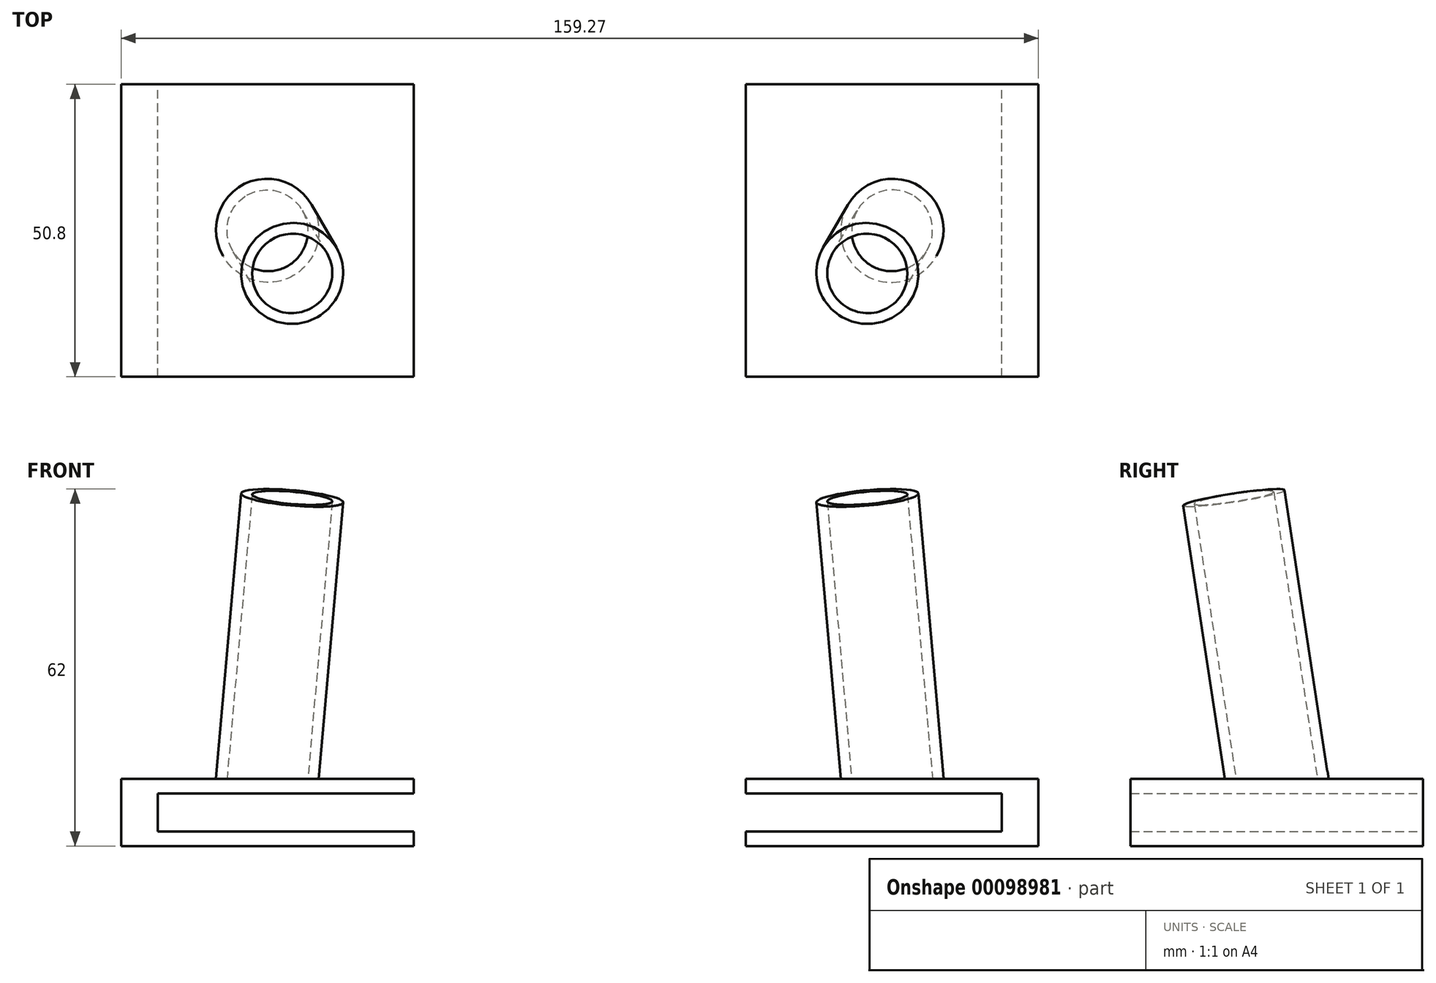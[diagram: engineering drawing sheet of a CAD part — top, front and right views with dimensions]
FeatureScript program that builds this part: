
annotation { "Feature Type Name" : "Feature", "Feature Type Description" : "" }
export const myFeature = defineFeature(function(context is Context, id is Id, definition is map)
    precondition{}
    {
        {
            var Q0;
            Q0=qCreatedBy(makeId("Top.planeOp"),FACE);
            var sketch = newSketch(context, id + "F0", { "sketchPlane" : qUnion([Q0])});
            skLineSegment(sketch, "E0.bottom", {"start": v(25.4, 25.4) * mm, "end": v(-25.4, 25.4) * mm});
            skLineSegment(sketch, "E0.top", {"start": v(25.4, -25.4) * mm, "end": v(-25.4, -25.4) * mm});
            skLineSegment(sketch, "E0.left", {"start": v(25.4, 25.4) * mm, "end": v(25.4, -25.4) * mm});
            skLineSegment(sketch, "E0.right", {"start": v(-25.4, 25.4) * mm, "end": v(-25.4, -25.4) * mm});
            skPoint(sketch, "E0.middle", {"position": v(0, 0) * mm});
            skSolve(sketch);
        }
        {
            var Q0;
            Q0=qSketchRegion(id+"F0",true);
            extrude(context, id + "F1", {"entities" : qUnion([Q0]), "oppositeDirection" : true, "depth" : 2.54 * mm});
        }
        {
            var Q0;
            Q0=makeQuery(id+"F1.opExtrude","CAP_FACE",FACE,{"disambiguationData":[OSD([sQuery(id+"F0.wireOp",EDGE,"E0.bottom"),sQuery(id+"F0.wireOp",EDGE,"E0.top"),sQuery(id+"F0.wireOp",EDGE,"E0.left"),sQuery(id+"F0.wireOp",EDGE,"E0.right")])],"isStart":false});
            var sketch = newSketch(context, id + "F2", { "sketchPlane" : qUnion([Q0])});
            skLineSegment(sketch, "E1.bottom", {"start": v(25.4, 25.4) * mm, "end": v(19.05, 25.4) * mm});
            skLineSegment(sketch, "E1.top", {"start": v(25.4, -25.4) * mm, "end": v(19.05, -25.4) * mm});
            skLineSegment(sketch, "E1.left", {"start": v(25.4, 25.4) * mm, "end": v(25.4, -25.4) * mm});
            skLineSegment(sketch, "E1.right", {"start": v(19.05, 25.4) * mm, "end": v(19.05, -25.4) * mm});
            skSolve(sketch);
        }
        {
            var Q0;
            Q0=qSketchRegion(id+"F2",true);
            extrude(context, id + "F3", {"entities" : qUnion([Q0]), "operationType" : NewBodyOperationType.ADD, "depth" : 6.6 * mm});
        }
        {
            var Q0;
            Q0=makeQuery(id+"F3.opExtrude","CAP_FACE",FACE,{"disambiguationData":[OSD([sQuery(id+"F2.wireOp",EDGE,"E1.bottom"),sQuery(id+"F2.wireOp",EDGE,"E1.top"),sQuery(id+"F2.wireOp",EDGE,"E1.left"),sQuery(id+"F2.wireOp",EDGE,"E1.right")])],"isStart":false});
            var sketch = newSketch(context, id + "F4", { "sketchPlane" : qUnion([Q0])});
            skLineSegment(sketch, "E2.bottom", {"start": v(25.4, 25.4) * mm, "end": v(-25.4, 25.4) * mm});
            skLineSegment(sketch, "E2.top", {"start": v(25.4, -25.4) * mm, "end": v(-25.4, -25.4) * mm});
            skLineSegment(sketch, "E2.left", {"start": v(25.4, 25.4) * mm, "end": v(25.4, -25.4) * mm});
            skLineSegment(sketch, "E2.right", {"start": v(-25.4, 25.4) * mm, "end": v(-25.4, -25.4) * mm});
            skSolve(sketch);
        }
        {
            var Q0;
            Q0=qSketchRegion(id+"F4",true);
            extrude(context, id + "F5", {"entities" : qUnion([Q0]), "operationType" : NewBodyOperationType.ADD, "depth" : 2.54 * mm});
        }
        {
            var Q0;
            Q0=makeQuery(id+"F1.opExtrude","CAP_FACE",FACE,{"disambiguationData":[OSD([sQuery(id+"F0.wireOp",EDGE,"E0.bottom"),sQuery(id+"F0.wireOp",EDGE,"E0.top"),sQuery(id+"F0.wireOp",EDGE,"E0.left"),sQuery(id+"F0.wireOp",EDGE,"E0.right")])],"isStart":true});
            var sketch = newSketch(context, id + "F6", { "sketchPlane" : qUnion([Q0])});
            skLineSegment(sketch, "E3", {"start": v(0, 25.4) * mm, "end": v(0, -28.09) * mm, "construction": true});
            skPoint(sketch, "E3.endSnap0", {"position": v(0, -25.4) * mm});
            skSolve(sketch);
        }
        {
            var Q0;
            Q0=qCreatedBy(makeId("Right.planeOp"),FACE);
            var sketch = newSketch(context, id + "F7", { "sketchPlane" : qUnion([Q0])});
            skLineSegment(sketch, "E4", {"start": v(0, 55.88) * mm, "end": v(0, -47.56) * mm, "construction": true});
            skSolve(sketch);
        }
        {
            var Q0;
            Q0=sQuery(id+"F6.wireOp",EDGE,"E3");
            cPlane(context, id + "F8", {"entities" : qUnion([Q0]), "cplaneType" : CPlaneType.LINE_ANGLE, "offset" : 152.4 * mm, "angle" : 10 * degree, "width" : 152.4 * mm, "height" : 152.4 * mm});
        }
        {
            var Q0;
            Q0=qCreatedBy(id+"F8.planeOp",FACE);
            var sketch = newSketch(context, id + "F9", { "sketchPlane" : qUnion([Q0])});
            skCircle(sketch, "E5", {"center": v(0, 0) * mm, "radius": 6.99 * mm});
            skCircle(sketch, "E6", {"center": v(0, 0) * mm, "radius": 8.9 * mm});
            skSolve(sketch);
        }
        {
            var Q0;
            Q0=qSketchRegion(id+"F9",true);
            extrude(context, id + "F10", {"entities" : qUnion([Q0]), "oppositeDirection" : true, "depth" : 49.53 * mm});
        }
        {
            var Q0;
            Q0=makeQuery(id+"F10.opExtrude","SWEPT_BODY",BODY,{"disambiguationData":[OSD([sQuery(id+"F9.wireOp",EDGE,"E5"),sQuery(id+"F9.wireOp",EDGE,"E6")])]});
            var Q1;
            Q1=sQuery(id+"F7.wireOp",EDGE,"E4");
            transform(context, id + "F11", {"entities" : qUnion([Q0]), "transformType" : TransformType.ROTATION, "transformAxis" : qUnion([Q1]), "angle" : 60 * degree, "oppositeDirection" : true, "makeCopy" : false});
        }
        {
            var Q0;
            Q0=qCreatedBy(makeId("Top.planeOp"),FACE);
            var sketch = newSketch(context, id + "F12", { "sketchPlane" : qUnion([Q0])});
            skLineSegment(sketch, "E7", {"start": v(-54.24, 36.53) * mm, "end": v(-54.24, -61.05) * mm, "construction": true});
            skSolve(sketch);
        }
        {
            var Q0;
            Q0=qCreatedBy(makeId("Right.planeOp"),FACE);
            var sketch = newSketch(context, id + "F13", { "sketchPlane" : qUnion([Q0])});
            skLineSegment(sketch, "E8", {"start": v(8.85, -52.8) * mm, "end": v(8.85, 70.73) * mm, "construction": true});
            skSolve(sketch);
        }
        {
            var Q0;
            Q0=sQuery(id+"F12.wireOp",EDGE,"E7");
            var Q1;
            Q1=sQuery(id+"F13.wireOp",EDGE,"E8");
            cPlane(context, id + "F14", {"entities" : qUnion([Q0, Q1]), "cplaneType" : CPlaneType.LINE_ANGLE, "offset" : 152.4 * mm, "angle" : 0 * degree, "width" : 152.4 * mm, "height" : 152.4 * mm});
        }
        {
            var Q0;
            Q0=makeQuery(id+"F10.opExtrude","CAP_FACE",FACE,{"disambiguationData":[OSD([sQuery(id+"F9.wireOp",EDGE,"E5"),sQuery(id+"F9.wireOp",EDGE,"E6")])],"isStart":false});
            var sketch = newSketch(context, id + "F15", { "sketchPlane" : qUnion([Q0])});
            skCircle(sketch, "E9", {"center": v(0, 0) * mm, "radius": 6.99 * mm});
            skCircle(sketch, "E10", {"center": v(0, 0) * mm, "radius": 8.9 * mm});
            skSolve(sketch);
        }
        {
            var Q0;
            Q0=qSketchRegion(id+"F15",true);
            var Q1;
            Q1=sQuery(id+"F15.wireOp",EDGE,"E10");
            var Q2;
            Q2=makeQuery(id+"F1.opExtrude","CAP_FACE",FACE,{"disambiguationData":[OSD([sQuery(id+"F0.wireOp",EDGE,"E0.bottom"),sQuery(id+"F0.wireOp",EDGE,"E0.top"),sQuery(id+"F0.wireOp",EDGE,"E0.left"),sQuery(id+"F0.wireOp",EDGE,"E0.right")])],"isStart":true});
            extrude(context, id + "F16", {"entities" : qUnion([Q0]), "operationType" : NewBodyOperationType.ADD, "surfaceEntities" : qUnion([Q1]), "endBound" : BoundingType.UP_TO_SURFACE, "oppositeDirection" : true, "endBoundEntityFace" : qUnion([Q2]), "depth" : 25.4 * mm});
        }
        {
            var Q0;
            Q0=makeQuery(id+"F10.opExtrude","SWEPT_BODY",BODY,{"disambiguationData":[OSD([sQuery(id+"F9.wireOp",EDGE,"E5"),sQuery(id+"F9.wireOp",EDGE,"E6")])]});
            var Q1;
            Q1=makeQuery(id+"F1.opExtrude","SWEPT_BODY",BODY,{"disambiguationData":[OSD([sQuery(id+"F0.wireOp",EDGE,"E0.bottom"),sQuery(id+"F0.wireOp",EDGE,"E0.top"),sQuery(id+"F0.wireOp",EDGE,"E0.left"),sQuery(id+"F0.wireOp",EDGE,"E0.right")])]});
            var Q2;
            Q2=qCreatedBy(id+"F14.planeOp",FACE);
            mirror(context, id + "F17", {"entities" : qUnion([Q0, Q1]), "mirrorPlane" : qUnion([Q2])});
        }
    });
